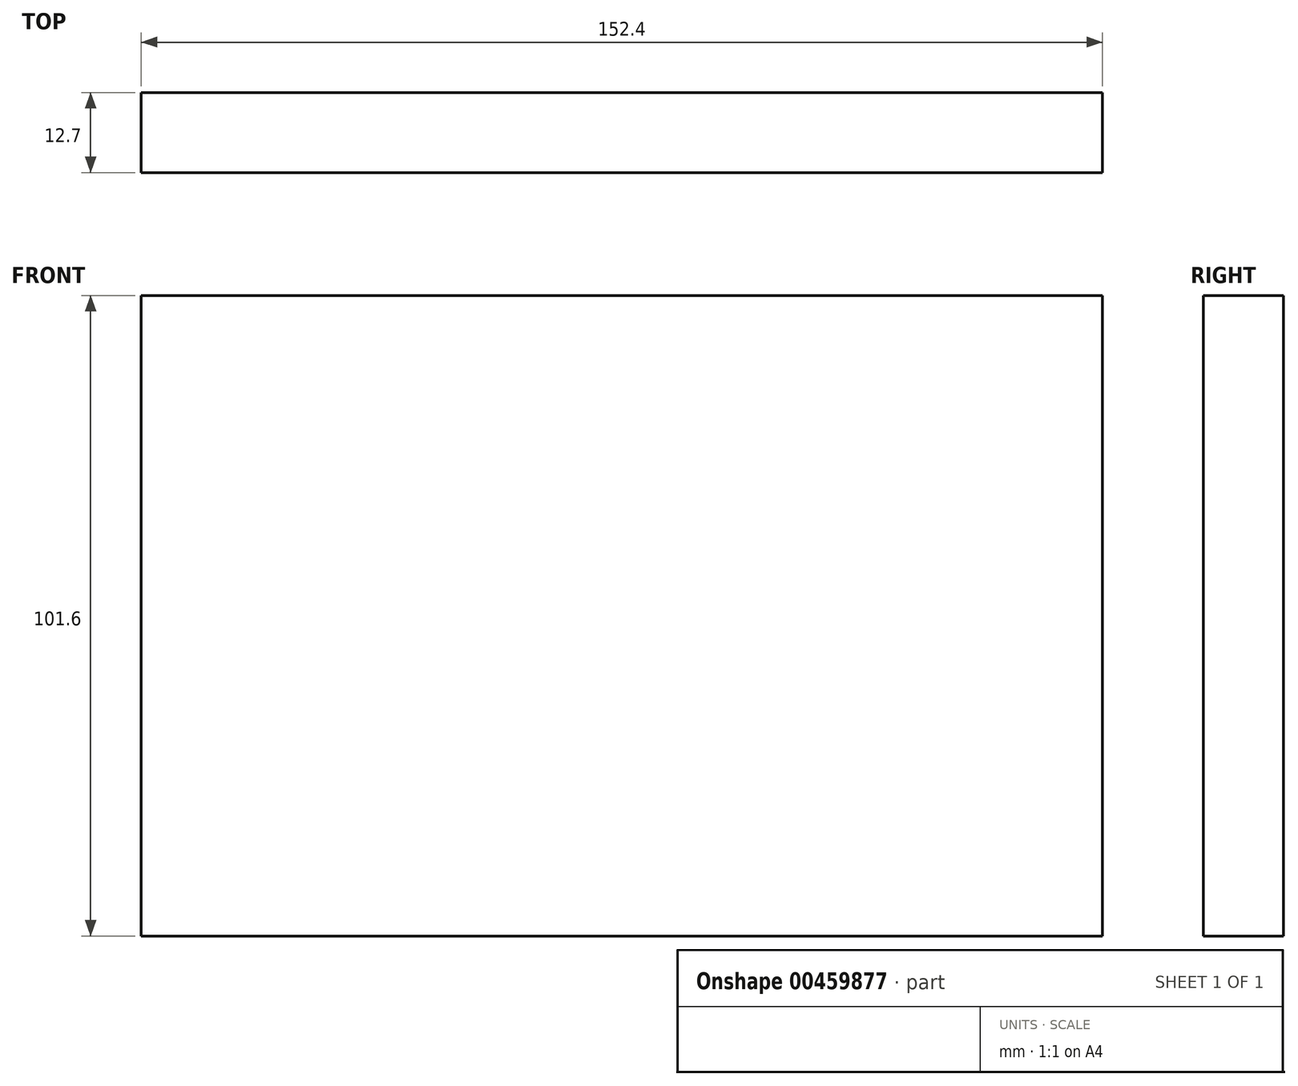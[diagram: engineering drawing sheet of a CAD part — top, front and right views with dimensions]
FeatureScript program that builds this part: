
annotation { "Feature Type Name" : "Feature", "Feature Type Description" : "" }
export const myFeature = defineFeature(function(context is Context, id is Id, definition is map)
    precondition{}
    {
        {
            var Q0;
            Q0=qCreatedBy(makeId("Front.planeOp"),FACE);
            var sketch = newSketch(context, id + "F0", { "sketchPlane" : qUnion([Q0])});
            skLineSegment(sketch, "E0.bottom", {"start": v(76.2, 50.8) * mm, "end": v(-76.2, 50.8) * mm});
            skLineSegment(sketch, "E0.top", {"start": v(76.2, -50.8) * mm, "end": v(-76.2, -50.8) * mm});
            skLineSegment(sketch, "E0.left", {"start": v(76.2, 50.8) * mm, "end": v(76.2, -50.8) * mm});
            skLineSegment(sketch, "E0.right", {"start": v(-76.2, 50.8) * mm, "end": v(-76.2, -50.8) * mm});
            skPoint(sketch, "E0.middle", {"position": v(0, 0) * mm});
            skSolve(sketch);
        }
        {
            var Q0;
            Q0=makeQuery(id+"F0.imprint","IMPRINT",FACE,{"disambiguationData":[TD([[makeQuery(id+"F0.imprint","IMPRINT",EDGE,{"derivedFrom":sQuery(id+"F0.wireOp",EDGE,"E0.bottom")}),1.0]])]});
            extrude(context, id + "F1", {"entities" : qUnion([Q0]), "depth" : 12.7 * mm});
        }
    });
